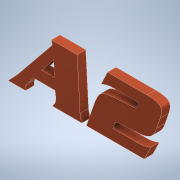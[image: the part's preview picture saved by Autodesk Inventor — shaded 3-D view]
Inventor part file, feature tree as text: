
AUTODESK INVENTOR PART (.ipt)
format: ipt  version: 2021 (Build 250183000, 183)  size: 151,552 bytes
history: native  units: mm
features: extrude x1, sketch x1
ambient origin geometry x8: Origin, YZ Plane, XZ Plane, XY Plane, X Axis, Y Axis, Z Axis, Center Point
bodies: Solid1 (feature_tree)
feature tree (2):
  extrude  "Extrusion1"  Depth=0.5mm
  sketch  "Sketch 1"  dims[d0=30.0mm d1=0.0mm d2=0.5mm d3=0.872665mm]
